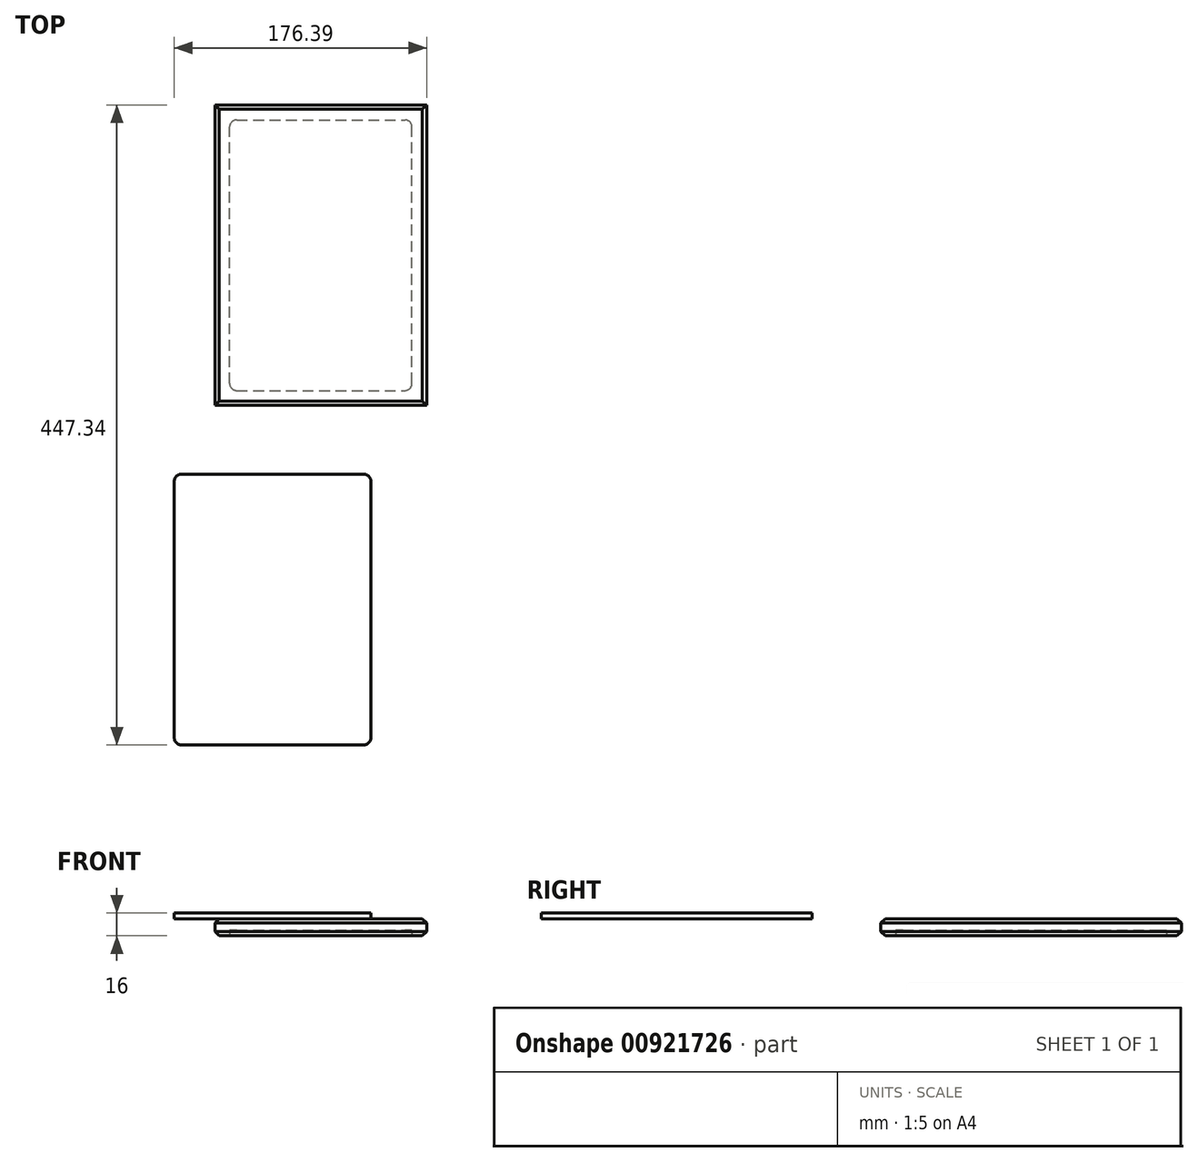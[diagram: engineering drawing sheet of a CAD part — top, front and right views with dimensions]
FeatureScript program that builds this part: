
annotation { "Feature Type Name" : "Feature", "Feature Type Description" : "" }
export const myFeature = defineFeature(function(context is Context, id is Id, definition is map)
    precondition{}
    {
        {
            var Q0;
            Q0=qCreatedBy(makeId("Top.planeOp"),FACE);
            var sketch = newSketch(context, id + "F0", { "sketchPlane" : qUnion([Q0])});
            skLineSegment(sketch, "E0.bottom", {"start": v(-74, -105) * mm, "end": v(74, -105) * mm});
            skLineSegment(sketch, "E0.top", {"start": v(-74, 105) * mm, "end": v(74, 105) * mm});
            skLineSegment(sketch, "E0.left", {"start": v(-74, -105) * mm, "end": v(-74, 105) * mm});
            skLineSegment(sketch, "E0.right", {"start": v(74, -105) * mm, "end": v(74, 105) * mm});
            skPoint(sketch, "E0.middle", {"position": v(0, 0) * mm});
            skSolve(sketch);
        }
        {
            var Q0;
            Q0 = qSketchRegion(id + "F0", true);
            extrude(context, id + "F1", {"entities" : qUnion([Q0]), "endBound" : BoundingType.SYMMETRIC, "depth" : 12 * mm, "offsetDistance" : 25 * mm});
        }
        {
            var Q0;
            Q0=makeQuery(id+"F1.opExtrude","CAP_EDGE",EDGE,{"disambiguationData":[OSD([sQuery(id+"F0.wireOp",EDGE,"E0.right")])],"isStart":false});
            var Q1;
            Q1=makeQuery(id+"F1.opExtrude","CAP_EDGE",EDGE,{"disambiguationData":[OSD([sQuery(id+"F0.wireOp",EDGE,"E0.right")])],"isStart":true});
            var Q2;
            Q2=makeQuery(id+"F1.opExtrude","CAP_EDGE",EDGE,{"disambiguationData":[OSD([sQuery(id+"F0.wireOp",EDGE,"E0.bottom")])],"isStart":true});
            var Q3;
            Q3=makeQuery(id+"F1.opExtrude","CAP_EDGE",EDGE,{"disambiguationData":[OSD([sQuery(id+"F0.wireOp",EDGE,"E0.bottom")])],"isStart":false});
            var Q4;
            Q4=makeQuery(id+"F1.opExtrude","CAP_EDGE",EDGE,{"disambiguationData":[OSD([sQuery(id+"F0.wireOp",EDGE,"E0.left")])],"isStart":false});
            var Q5;
            Q5=makeQuery(id+"F1.opExtrude","CAP_EDGE",EDGE,{"disambiguationData":[OSD([sQuery(id+"F0.wireOp",EDGE,"E0.left")])],"isStart":true});
            var Q6;
            Q6=makeQuery(id+"F1.opExtrude","CAP_EDGE",EDGE,{"disambiguationData":[OSD([sQuery(id+"F0.wireOp",EDGE,"E0.top")])],"isStart":true});
            var Q7;
            Q7=makeQuery(id+"F1.opExtrude","CAP_EDGE",EDGE,{"disambiguationData":[OSD([sQuery(id+"F0.wireOp",EDGE,"E0.top")])],"isStart":false});
            chamfer(context, id + "F2", {"entities" : qUnion([Q0, Q1, Q2, Q3, Q4, Q5, Q6, Q7]), "width" : 3 * mm, "tangentPropagation" : true});
        }
        {
            var Q0;
            Q0=makeQuery(id+"F1.opExtrude","CAP_FACE",FACE,{"disambiguationData":[OSD([sQuery(id+"F0.wireOp",EDGE,"E0.bottom"),sQuery(id+"F0.wireOp",EDGE,"E0.top"),sQuery(id+"F0.wireOp",EDGE,"E0.left"),sQuery(id+"F0.wireOp",EDGE,"E0.right")])],"isStart":true});
            var sketch = newSketch(context, id + "F3", { "sketchPlane" : qUnion([Q0])});
            skLineSegment(sketch, "E1.bottom", {"start": v(-58.7, 94.63) * mm, "end": v(58.7, 94.63) * mm});
            skLineSegment(sketch, "E1.top", {"start": v(-58.7, -94.63) * mm, "end": v(58.7, -94.63) * mm});
            skLineSegment(sketch, "E1.left", {"start": v(-63.7, 89.63) * mm, "end": v(-63.7, -89.63) * mm});
            skLineSegment(sketch, "E1.right", {"start": v(63.7, 89.63) * mm, "end": v(63.7, -89.63) * mm});
            skPoint(sketch, "E1.middle", {"position": v(0, 0) * mm});
            skPoint(sketch, "E2.visualSharp", {"position": v(-63.7, 94.63) * mm});
            skArc(sketch, "E2.filletArc", {"start": v(-58.7, 94.63) * mm, "mid": v(-62.24, 93.17) * mm, "end": v(-63.7, 89.63) * mm});
            skPoint(sketch, "E3.visualSharp", {"position": v(63.7, 94.63) * mm});
            skArc(sketch, "E3.filletArc", {"start": v(63.7, 89.63) * mm, "mid": v(62.24, 93.17) * mm, "end": v(58.7, 94.63) * mm});
            skPoint(sketch, "E4.visualSharp", {"position": v(63.7, -94.63) * mm});
            skArc(sketch, "E4.filletArc", {"start": v(58.7, -94.63) * mm, "mid": v(62.24, -93.17) * mm, "end": v(63.7, -89.63) * mm});
            skPoint(sketch, "E5.visualSharp", {"position": v(-63.7, -94.63) * mm});
            skArc(sketch, "E5.filletArc", {"start": v(-63.7, -89.63) * mm, "mid": v(-62.24, -93.17) * mm, "end": v(-58.7, -94.63) * mm});
            skSolve(sketch);
        }
        {
            var Q0;
            Q0 = qSketchRegion(id + "F3", true);
            extrude(context, id + "F4", {"entities" : qUnion([Q0]), "operationType" : NewBodyOperationType.REMOVE, "oppositeDirection" : true, "depth" : 4 * mm, "offsetDistance" : 25 * mm});
        }
        {
            var Q0;
            Q0=makeQuery(id+"F1.opExtrude","CAP_FACE",FACE,{"disambiguationData":[OSD([sQuery(id+"F0.wireOp",EDGE,"E0.bottom"),sQuery(id+"F0.wireOp",EDGE,"E0.top"),sQuery(id+"F0.wireOp",EDGE,"E0.left"),sQuery(id+"F0.wireOp",EDGE,"E0.right")])],"isStart":false});
            var sketch = newSketch(context, id + "F5", { "sketchPlane" : qUnion([Q0])});
            skLineSegment(sketch, "E6.bottom", {"start": v(-97.39, -153.07) * mm, "end": v(30.03, -153.07) * mm});
            skLineSegment(sketch, "E6.top", {"start": v(-97.39, -342.34) * mm, "end": v(30.03, -342.34) * mm});
            skLineSegment(sketch, "E6.left", {"start": v(-102.39, -158.07) * mm, "end": v(-102.39, -337.34) * mm});
            skLineSegment(sketch, "E6.right", {"start": v(35.03, -158.07) * mm, "end": v(35.03, -337.34) * mm});
            skPoint(sketch, "E6.middle", {"position": v(-33.68, -247.7) * mm});
            skPoint(sketch, "E7.visualSharp", {"position": v(-102.39, -153.07) * mm});
            skArc(sketch, "E7.filletArc", {"start": v(-97.39, -153.07) * mm, "mid": v(-100.92, -154.54) * mm, "end": v(-102.39, -158.07) * mm});
            skPoint(sketch, "E8.visualSharp", {"position": v(35.03, -153.07) * mm});
            skArc(sketch, "E8.filletArc", {"start": v(35.03, -158.07) * mm, "mid": v(33.56, -154.54) * mm, "end": v(30.03, -153.07) * mm});
            skPoint(sketch, "E9.visualSharp", {"position": v(35.03, -342.34) * mm});
            skArc(sketch, "E9.filletArc", {"start": v(30.03, -342.34) * mm, "mid": v(33.56, -340.87) * mm, "end": v(35.03, -337.34) * mm});
            skPoint(sketch, "E10.visualSharp", {"position": v(-102.39, -342.34) * mm});
            skArc(sketch, "E10.filletArc", {"start": v(-102.39, -337.34) * mm, "mid": v(-100.92, -340.87) * mm, "end": v(-97.39, -342.34) * mm});
            skLineSegment(sketch, "E11.bottom", {"start": v(-58.7, 94.63) * mm, "end": v(58.7, 94.63) * mm});
            skLineSegment(sketch, "E11.top", {"start": v(-58.7, -94.63) * mm, "end": v(58.7, -94.63) * mm});
            skLineSegment(sketch, "E11.left", {"start": v(-63.7, 89.63) * mm, "end": v(-63.7, -89.63) * mm});
            skLineSegment(sketch, "E11.right", {"start": v(63.7, 89.63) * mm, "end": v(63.7, -89.63) * mm});
            skPoint(sketch, "E11.middle", {"position": v(0, 0) * mm});
            skPoint(sketch, "E12.visualSharp", {"position": v(-63.7, 94.63) * mm});
            skArc(sketch, "E12.filletArc", {"start": v(-58.7, 94.63) * mm, "mid": v(-62.24, 93.17) * mm, "end": v(-63.7, 89.63) * mm});
            skPoint(sketch, "E13.visualSharp", {"position": v(63.7, 94.63) * mm});
            skArc(sketch, "E13.filletArc", {"start": v(63.7, 89.63) * mm, "mid": v(62.24, 93.17) * mm, "end": v(58.7, 94.63) * mm});
            skPoint(sketch, "E14.visualSharp", {"position": v(63.7, -94.63) * mm});
            skArc(sketch, "E14.filletArc", {"start": v(58.7, -94.63) * mm, "mid": v(62.24, -93.17) * mm, "end": v(63.7, -89.63) * mm});
            skPoint(sketch, "E15.visualSharp", {"position": v(-63.7, -94.63) * mm});
            skArc(sketch, "E15.filletArc", {"start": v(-63.7, -89.63) * mm, "mid": v(-62.24, -93.17) * mm, "end": v(-58.7, -94.63) * mm});
            skSolve(sketch);
        }
        {
            var Q0;
            Q0=makeQuery(id+"F5.imprint","IMPRINT",FACE,{"disambiguationData":[TD([[makeQuery(id+"F5.imprint","IMPRINT",EDGE,{"derivedFrom":sQuery(id+"F5.wireOp",EDGE,"E6.bottom")}),-1.0]])]});
            extrude(context, id + "F6", {"entities" : qUnion([Q0]), "depth" : 4 * mm, "offsetDistance" : 25 * mm});
        }
    });
